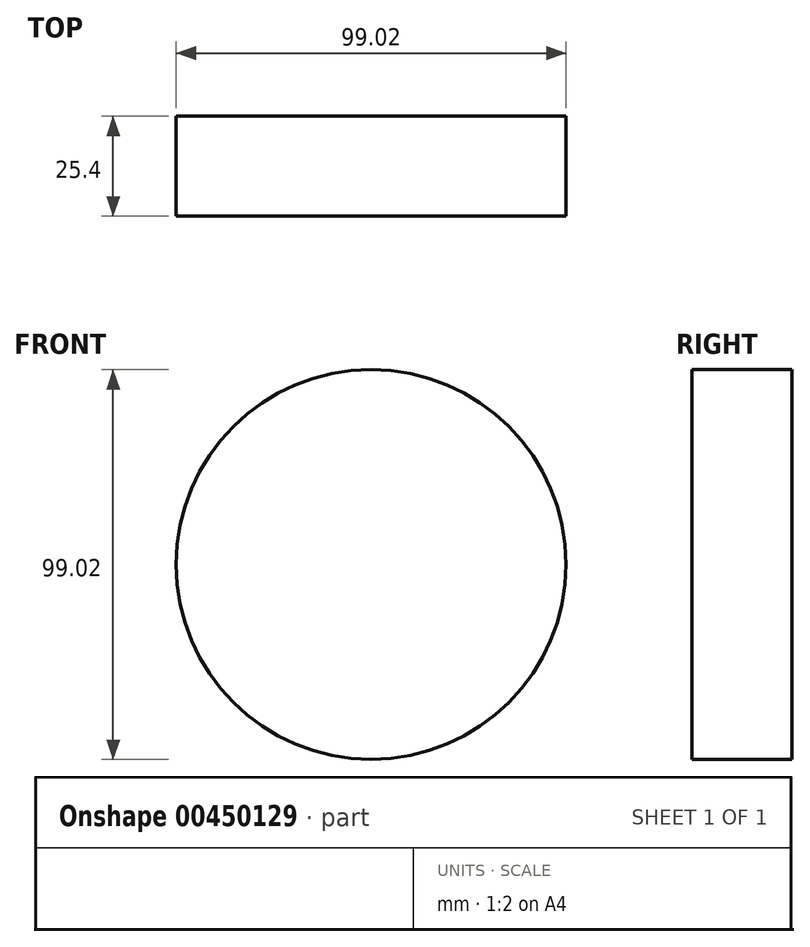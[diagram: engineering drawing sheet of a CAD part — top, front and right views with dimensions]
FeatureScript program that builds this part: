
annotation { "Feature Type Name" : "Feature", "Feature Type Description" : "" }
export const myFeature = defineFeature(function(context is Context, id is Id, definition is map)
    precondition{}
    {
        {
            var Q0;
            Q0=qCreatedBy(makeId("Front.planeOp"),FACE);
            var sketch = newSketch(context, id + "F0", { "sketchPlane" : qUnion([Q0])});
            skCircle(sketch, "E0", {"center": v(0, 0) * mm, "radius": 49.51 * mm});
            skSolve(sketch);
        }
        {
            var Q0;
            Q0=makeQuery(id+"F0.imprint","IMPRINT",FACE,{"disambiguationData":[TD([[makeQuery(id+"F0.imprint","IMPRINT",EDGE,{"derivedFrom":sQuery(id+"F0.wireOp",EDGE,"E0")}),1.0]])]});
            extrude(context, id + "F1", {"entities" : qUnion([Q0]), "depth" : 25.4 * mm});
        }
    });
